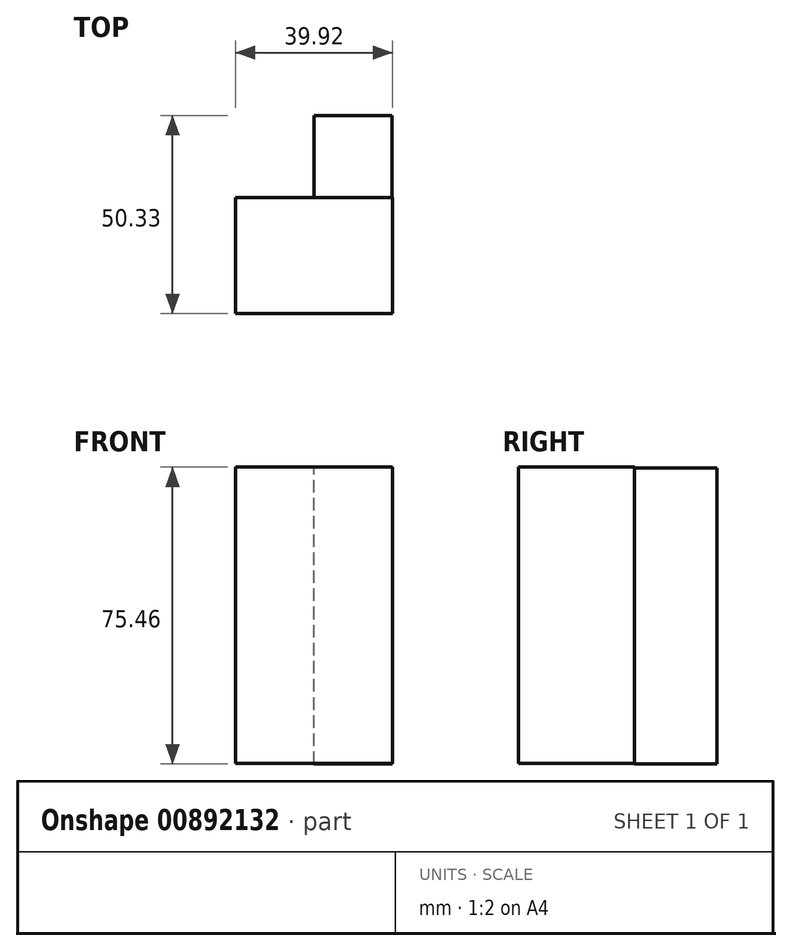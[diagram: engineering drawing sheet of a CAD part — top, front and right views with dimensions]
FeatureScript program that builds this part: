
annotation { "Feature Type Name" : "Feature", "Feature Type Description" : "" }
export const myFeature = defineFeature(function(context is Context, id is Id, definition is map)
    precondition{}
    {
        {
            var Q0;
            Q0=qCreatedBy(makeId("Front.planeOp"),FACE);
            var sketch = newSketch(context, id + "F0", { "sketchPlane" : qUnion([Q0])});
            skLineSegment(sketch, "E0.bottom", {"start": v(-19.96, 37.64) * mm, "end": v(19.96, 37.64) * mm});
            skLineSegment(sketch, "E0.top", {"start": v(-19.96, -37.64) * mm, "end": v(19.96, -37.64) * mm});
            skLineSegment(sketch, "E0.left", {"start": v(-19.96, 37.64) * mm, "end": v(-19.96, -37.64) * mm});
            skLineSegment(sketch, "E0.right", {"start": v(19.96, 37.64) * mm, "end": v(19.96, -37.64) * mm});
            skPoint(sketch, "E0.middle", {"position": v(0, 0) * mm});
            skSolve(sketch);
        }
        {
            var Q0;
            Q0=makeQuery(id+"F0.imprint","IMPRINT",FACE,{"disambiguationData":[TD([[makeQuery(id+"F0.imprint","IMPRINT",EDGE,{"derivedFrom":sQuery(id+"F0.wireOp",EDGE,"E0.bottom")}),-1.0]])]});
            var sketch = newSketch(context, id + "F1", { "sketchPlane" : qUnion([Q0])});
            skSolve(sketch);
        }
        {
            var Q0;
            Q0 = qSketchRegion(id + "F1", true);
            var Q1;
            Q1=makeQuery(id+"F1.imprint","IMPRINT",FACE,{"disambiguationData":[TD([[makeQuery(id+"F1.imprint","IMPRINT",EDGE,{"derivedFrom":makeQuery(id+"F0.imprint","IMPRINT",EDGE,{"derivedFrom":sQuery(id+"F0.wireOp",EDGE,"E0.bottom")})}),-1.0]])]});
            extrude(context, id + "F2", {"entities" : qUnion([Q0, Q1]), "depth" : 29.46 * mm, "offsetDistance" : 25.4 * mm});
        }
        {
            var Q0;
            Q0=qCreatedBy(makeId("Right.planeOp"),FACE);
            var sketch = newSketch(context, id + "F3", { "sketchPlane" : qUnion([Q0])});
            skLineSegment(sketch, "E1.bottom", {"start": v(0, -37.82) * mm, "end": v(20.87, -37.82) * mm});
            skLineSegment(sketch, "E1.top", {"start": v(0, 37.45) * mm, "end": v(20.87, 37.45) * mm});
            skLineSegment(sketch, "E1.left", {"start": v(0, -37.82) * mm, "end": v(0, 37.45) * mm});
            skLineSegment(sketch, "E1.right", {"start": v(20.87, -37.82) * mm, "end": v(20.87, 37.45) * mm});
            skSolve(sketch);
        }
        {
            var Q0;
            Q0=makeQuery(id+"F3.imprint","IMPRINT",FACE,{"disambiguationData":[TD([[makeQuery(id+"F3.imprint","IMPRINT",EDGE,{"derivedFrom":sQuery(id+"F3.wireOp",EDGE,"E1.bottom")}),1.0]])]});
            extrude(context, id + "F4", {"entities" : qUnion([Q0]), "operationType" : NewBodyOperationType.ADD, "depth" : 19.8 * mm, "offsetDistance" : 25.4 * mm});
        }
    });
